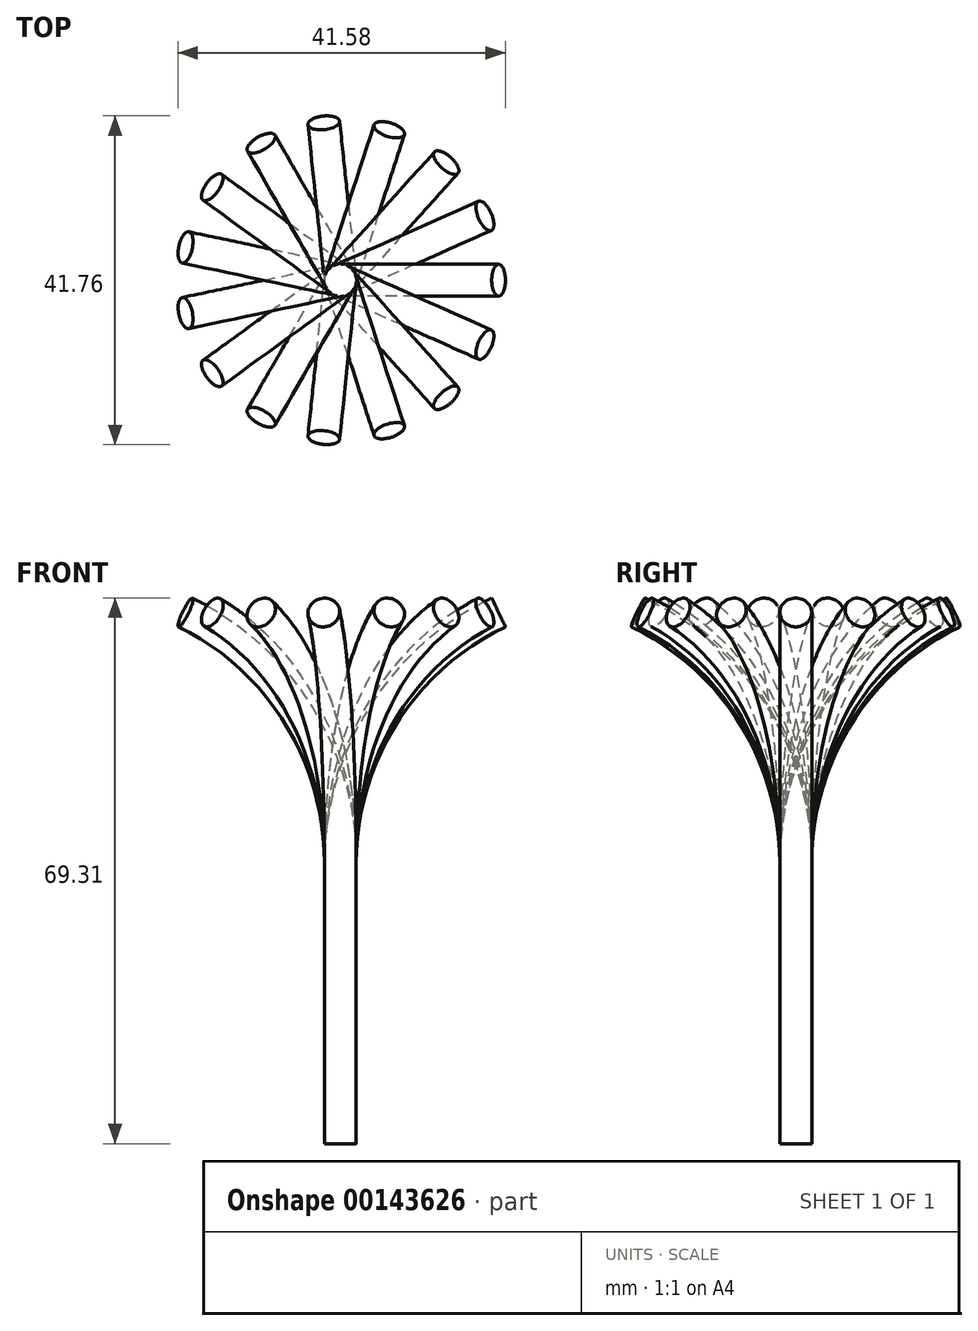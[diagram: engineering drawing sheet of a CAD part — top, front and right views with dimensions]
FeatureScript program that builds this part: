
annotation { "Feature Type Name" : "Feature", "Feature Type Description" : "" }
export const myFeature = defineFeature(function(context is Context, id is Id, definition is map)
    precondition{}
    {
        {
            var Q0;
            Q0=qCreatedBy(makeId("Top.planeOp"),FACE);
            var sketch = newSketch(context, id + "F0", { "sketchPlane" : qUnion([Q0])});
            skCircle(sketch, "E0", {"center": v(0, 0) * mm, "radius": 2.02 * mm});
            skSolve(sketch);
        }
        {
            var Q0;
            Q0=qCreatedBy(makeId("Front.planeOp"),FACE);
            var sketch = newSketch(context, id + "F1", { "sketchPlane" : qUnion([Q0])});
            skLineSegment(sketch, "E1", {"start": v(0, 0) * mm, "end": v(0, 35.63) * mm});
            skArc(sketch, "E2", {"start": v(0, 35.63) * mm, "mid": v(5.45, 54.46) * mm, "end": v(20.1, 67.48) * mm});
            skSolve(sketch);
        }
        {
            var Q0;
            Q0=makeQuery(id+"F0.imprint","IMPRINT",FACE,{"disambiguationData":[TD([[makeQuery(id+"F0.imprint","IMPRINT",EDGE,{"derivedFrom":sQuery(id+"F0.wireOp",EDGE,"E0")}),1.0]])]});
            var Q1;
            Q1=sQuery(id+"F1.wireOp",EDGE,"E2");
            var Q2;
            Q2=sQuery(id+"F1.wireOp",EDGE,"E1");
            sweep(context, id + "F2", {"profiles" : qUnion([Q0]), "path" : qUnion([Q1, Q2])});
        }
        {
            var Q0;
            Q0=makeQuery(id+"F2.opSweep","SWEPT_BODY",BODY,{"disambiguationData":[OSD([sQuery(id+"F0.wireOp",EDGE,"E0"),sQuery(id+"F1.wireOp",EDGE,"E1")])]});
            var Q1;
            Q1=makeQuery(id+"F2.opSweep","CAP_EDGE",EDGE,{"disambiguationData":[OSD([sQuery(id+"F0.wireOp",EDGE,"E0"),sQuery(id+"F1.wireOp",VERTEX,"E1.start")])],"isStart":true});
            circularPattern(context, id + "F3", {"entities" : qUnion([Q0]), "axis" : qUnion([Q1]), "angle" : 360 * degree, "instanceCount" : 15, "equalSpace" : true});
        }
    });
